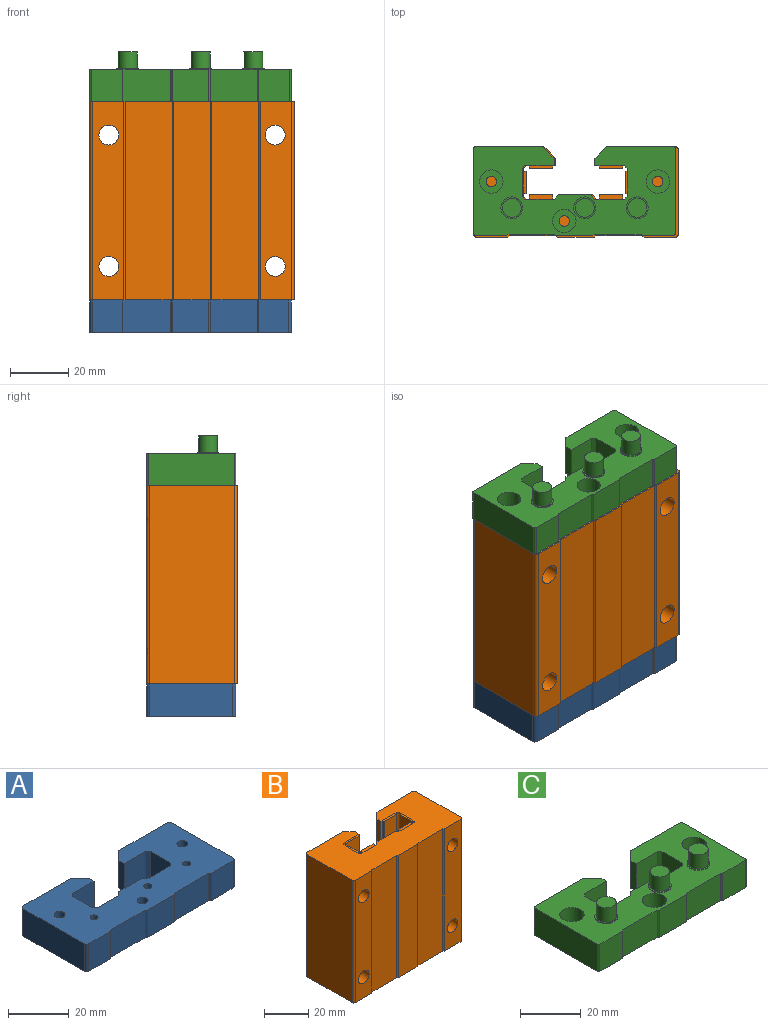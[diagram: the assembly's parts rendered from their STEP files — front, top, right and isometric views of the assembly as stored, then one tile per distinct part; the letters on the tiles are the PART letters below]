
ASSEMBLY  parts=3 mates=6
PART A: 51 faces, bbox 69x30.5x11 mm
  f0: cylinder r=1.8mm len=5mm, axis (0,0,1), area 56.5mm2, adj f49,f50
  f1: cylinder r=4mm len=8mm, axis (0,0,1), area 150.8mm2, adj f14,f50
  f2: cylinder r=1.8mm len=5mm, axis (0,0,1), area 56.5mm2, adj f13,f49
  f3: cylinder r=1.8mm len=5mm, axis (0,0,1), area 56.5mm2, adj f12,f49
  f4: cylinder r=1.3mm len=10mm, axis (0,0,1), area 81.7mm2, adj f7,f49
  f5: cylinder r=1.3mm len=10mm, axis (0,0,1), area 81.7mm2, adj f8,f49
  f6: cylinder r=1.3mm len=10mm, axis (0,0,1), area 81.7mm2, adj f9,f49
  f7: cone r=0.94mm half-angle=30deg, axis (0,0,-1), area 11.5mm2, adj f4,f14
  f8: cone r=0.94mm half-angle=30deg, axis (0,0,-1), area 11.5mm2, adj f5,f14
  f9: cone r=0.94mm half-angle=30deg, axis (0,0,-1), area 11.5mm2, adj f6,f14
  f10: cylinder r=4mm len=8mm, axis (0,0,1), area 150.8mm2, adj f13,f14
  f11: cylinder r=4mm len=8mm, axis (0,0,1), area 150.8mm2, adj f12,f14
  f12: plane 8x8mm, normal (0,0,-1), area 40.1mm2, adj f3,f11
  f13: plane 8x8mm, normal (0,0,-1), area 40.1mm2, adj f2,f10
  f14: plane 69x30.5mm, normal (0,0,-1), area 1402.9mm2, adj f1,f7,f8,f9,f10,f11,f15,f16
  f15: plane 11x2.5mm, normal (1,0,0), area 27.5mm2, adj f14,f16,f48,f49
  f16: plane 11x10mm, normal (0,-1,0), area 110mm2, adj f14,f15,f17,f49
  f17: plane 11x1mm, normal (0.71,-0.71,0), area 15.6mm2, adj f14,f16,f18,f49
  f18: plane 11x9.5mm, normal (1,0,0), area 104.5mm2, adj f14,f17,f19,f49
  f19: plane 11x1mm, normal (0.71,0.71,0), area 15.6mm2, adj f14,f18,f20,f49
  f20: plane 11x10mm, normal (0,1,0), area 110mm2, adj f14,f19,f21,f49
  f21: plane 11x1.5mm, normal (-0.71,0.71,0), area 23.3mm2, adj f14,f20,f22,f49
  f22: plane 11x11mm, normal (0,1,0), area 121mm2, adj f14,f21,f23,f49
  f23: plane 11x1.5mm, normal (0.71,0.71,0), area 23.3mm2, adj f14,f22,f24,f49
  f24: plane 11x10mm, normal (0,1,0), area 110mm2, adj f14,f23,f25,f49
  f25: plane 11x1mm, normal (-0.71,0.71,0), area 15.6mm2, adj f14,f24,f26,f49
  f26: plane 11x9.5mm, normal (-1,0,0), area 104.5mm2, adj f14,f25,f27,f49
  f27: plane 11x1mm, normal (-0.71,-0.71,0), area 15.6mm2, adj f14,f26,f28,f49
  f28: plane 11x10mm, normal (0,-1,0), area 110mm2, adj f14,f27,f29,f49
  f29: plane 11x2.5mm, normal (-1,0,0), area 27.5mm2, adj f14,f28,f30,f49
  f30: plane 11x4mm, normal (-0.71,0.71,0), area 62.2mm2, adj f14,f29,f31,f49
  f31: plane 22.5x11mm, normal (0,1,0), area 247.5mm2, adj f14,f30,f32,f49
  f32: cylinder r=1mm len=11mm, axis (0,0,1), area 17.3mm2, adj f14,f31,f33,f49
  f33: plane 28.5x11mm, normal (1,0,0), area 313.5mm2, adj f14,f32,f34,f49
  f34: cylinder r=1mm len=11mm, axis (0,0,1), area 17.3mm2, adj f14,f33,f35,f49
  f35: plane 11x10.2mm, normal (0,-1,0), area 112.2mm2, adj f14,f34,f36,f49
  f36: plane 11x0.5mm, normal (-0.71,-0.71,0), area 7.8mm2, adj f14,f35,f37,f49
  f37: plane 16x11mm, normal (0,-1,0), area 176mm2, adj f14,f36,f38,f49
  f38: plane 11x0.5mm, normal (0.71,-0.71,0), area 7.8mm2, adj f14,f37,f39,f49
  f39: plane 12.6x11mm, normal (0,-1,0), area 138.6mm2, adj f14,f38,f40,f49
  f40: plane 11x0.5mm, normal (-0.71,-0.71,0), area 7.8mm2, adj f14,f39,f41,f49
  f41: plane 16x11mm, normal (0,-1,0), area 176mm2, adj f14,f40,f42,f49
  f42: plane 11x0.5mm, normal (0.71,-0.71,0), area 7.8mm2, adj f14,f41,f43,f49
  f43: plane 11x10.2mm, normal (0,-1,0), area 112.2mm2, adj f14,f42,f44,f49
  f44: cylinder r=1mm len=11mm, axis (0,0,1), area 17.3mm2, adj f14,f43,f45,f49
  f45: plane 28.5x11mm, normal (-1,0,0), area 313.5mm2, adj f14,f44,f46,f49
  f46: cylinder r=1mm len=11mm, axis (0,0,1), area 17.3mm2, adj f14,f45,f47,f49
  f47: plane 22.5x11mm, normal (0,1,0), area 247.5mm2, adj f14,f46,f48,f49
  f48: plane 11x4mm, normal (0.71,0.71,0), area 62.2mm2, adj f14,f15,f47,f49
  f49: plane 69x30.5mm, normal (0,0,1), area 1540.4mm2, adj f0,f2,f3,f4,f5,f6,f15,f16
  f50: plane 8x8mm, normal (0,0,-1), area 40.1mm2, adj f0,f1
PART B: 78 faces, bbox 70x31x68 mm
  f0: cylinder r=6mm len=12mm, axis (0,-1,0), area 233.4mm2, adj f16,f40,f73
  f1: cylinder r=6mm len=12mm, axis (0,-1,0), area 233.4mm2, adj f15,f40,f73
  f2: cylinder r=6mm len=12mm, axis (0,-1,0), area 233.4mm2, adj f9,f54,f55
  f3: cylinder r=6mm len=12mm, axis (0,-1,0), area 233.4mm2, adj f8,f54,f55
  f4: cylinder r=3.4mm len=24.8mm, axis (0,-1,0), area 529.8mm2, adj f9,f51
  f5: cylinder r=3.4mm len=24.8mm, axis (0,-1,0), area 529.8mm2, adj f8,f51
  f6: cylinder r=3.4mm len=24.8mm, axis (0,-1,0), area 529.8mm2, adj f16,f43
  f7: cylinder r=3.4mm len=24.8mm, axis (0,-1,0), area 529.8mm2, adj f15,f43
  f8: plane 12x12mm, normal (0,1,0), area 76.8mm2, adj f3,f5
  f9: plane 12x12mm, normal (0,1,0), area 76.8mm2, adj f2,f4
  f10: plane 68x8mm, normal (0,-1,0), area 544mm2, adj f17,f18,f19,f20
  f11: plane 68x7.5mm, normal (1,0,0), area 510mm2, adj f21,f22,f23,f24
  f12: plane 68x8mm, normal (0,1,0), area 544mm2, adj f25,f26,f27,f28
  f13: plane 68x8mm, normal (0,1,0), area 544mm2, adj f29,f30,f31,f32
  f14: plane 68x8mm, normal (0,-1,0), area 544mm2, adj f33,f34,f35,f36
  f15: plane 12x12mm, normal (0,1,0), area 76.8mm2, adj f1,f7
  f16: plane 12x12mm, normal (0,1,0), area 76.8mm2, adj f0,f6
  f17: plane 8x1mm, normal (0,0,1), area 8mm2, adj f10,f19,f20,f77
  f18: plane 8x1mm, normal (0,0,-1), area 8mm2, adj f10,f19,f20,f58
  f19: plane 68x1mm, normal (1,0,0), area 68mm2, adj f10,f17,f18,f58
  f20: plane 68x1mm, normal (-1,0,0), area 68mm2, adj f10,f17,f18,f58
  f21: plane 7.5x1mm, normal (0,0,1), area 7.5mm2, adj f11,f23,f24,f77
  f22: plane 7.5x1mm, normal (0,0,-1), area 7.5mm2, adj f11,f23,f24,f60
  f23: plane 68x1mm, normal (0,1,0), area 68mm2, adj f11,f21,f22,f60
  f24: plane 68x1mm, normal (0,-1,0), area 68mm2, adj f11,f21,f22,f60
  f25: plane 8x1.5mm, normal (0,0,1), area 12mm2, adj f12,f27,f28,f77
  f26: plane 8x1.5mm, normal (0,0,-1), area 12mm2, adj f12,f27,f28,f62
  f27: plane 68x1.5mm, normal (-1,0,0), area 102mm2, adj f12,f25,f26,f62
  f28: plane 68x1.5mm, normal (1,0,0), area 102mm2, adj f12,f25,f26,f62
  f29: plane 8x1.5mm, normal (0,0,1), area 12mm2, adj f13,f31,f32,f77
  f30: plane 8x1.5mm, normal (0,0,-1), area 12mm2, adj f13,f31,f32,f66
  f31: plane 68x1.5mm, normal (-1,0,0), area 102mm2, adj f13,f29,f30,f66
  f32: plane 68x1.5mm, normal (1,0,0), area 102mm2, adj f13,f29,f30,f66
  f33: plane 8x1mm, normal (0,0,1), area 8mm2, adj f14,f35,f36,f77
  f34: plane 8x1mm, normal (0,0,-1), area 8mm2, adj f14,f35,f36,f70
  f35: plane 68x1mm, normal (1,0,0), area 68mm2, adj f14,f33,f34,f70
  f36: plane 68x1mm, normal (-1,0,0), area 68mm2, adj f14,f33,f34,f70
  f37: plane 70x31mm, normal (0,0,-1), area 1652.4mm2, adj f40,f41,f42,f43,f44,f45,f46,f47
  f38: plane 68x7.5mm, normal (-1,0,0), area 510mm2, adj f39,f74,f75,f76
  f39: plane 7.5x1mm, normal (0,0,-1), area 7.5mm2, adj f38,f68,f74,f76
  f40: cylinder r=1mm len=68mm, axis (0,0,-1), area 104.3mm2, adj f0,f1,f37,f41,f73,f77
  f41: plane 68x29mm, normal (1,0,0), area 1972mm2, adj f37,f40,f42,f77
  f42: cylinder r=1mm len=68mm, axis (0,0,-1), area 106.8mm2, adj f37,f41,f43,f77
  f43: plane 68x10.7mm, normal (0,-1,0), area 655mm2, adj f6,f7,f37,f42,f44,f77
  f44: plane 68x0.5mm, normal (-0.71,-0.71,0), area 48.1mm2, adj f37,f43,f45,f77
  f45: plane 68x16mm, normal (0,-1,0), area 1088mm2, adj f37,f44,f46,f77
  f46: plane 68x0.5mm, normal (0.71,-0.71,0), area 48.1mm2, adj f37,f45,f47,f77
  f47: plane 68x12.6mm, normal (0,-1,0), area 856.8mm2, adj f37,f46,f48,f77
  f48: plane 68x0.5mm, normal (-0.71,-0.71,0), area 48.1mm2, adj f37,f47,f49,f77
  f49: plane 68x16mm, normal (0,-1,0), area 1088mm2, adj f37,f48,f50,f77
  f50: plane 68x0.5mm, normal (0.71,-0.71,0), area 48.1mm2, adj f37,f49,f51,f77
  f51: plane 68x10.7mm, normal (0,-1,0), area 655mm2, adj f4,f5,f37,f50,f52,f77
  f52: cylinder r=1mm len=68mm, axis (0,0,-1), area 106.8mm2, adj f37,f51,f53,f77
  f53: plane 68x29mm, normal (-1,0,0), area 1972mm2, adj f37,f52,f54,f77
  f54: cylinder r=1mm len=68mm, axis (0,0,-1), area 104.3mm2, adj f2,f3,f37,f53,f55,f77
  f55: plane 68x23mm, normal (0,1,0), area 1341mm2, adj f2,f3,f37,f54,f56,f77
  f56: plane 68x4mm, normal (0.71,0.71,0), area 384.7mm2, adj f37,f55,f57,f77
  f57: plane 68x2.5mm, normal (1,0,0), area 170mm2, adj f37,f56,f58,f77
  f58: plane 68x10mm, normal (0,-1,0), area 136mm2, adj f18,f19,f20,f37,f57,f59,f77
  f59: plane 68x1mm, normal (0.71,-0.71,0), area 96.2mm2, adj f37,f58,f60,f77
  f60: plane 68x9.5mm, normal (1,0,0), area 136mm2, adj f22,f23,f24,f37,f59,f61,f77
  f61: plane 68x1mm, normal (0.71,0.71,0), area 96.2mm2, adj f37,f60,f62,f77
  f62: plane 68x10mm, normal (0,1,0), area 136mm2, adj f26,f27,f28,f37,f61,f63,f77
  f63: plane 68x1.5mm, normal (-0.71,0.71,0), area 144.2mm2, adj f37,f62,f64,f77
  f64: plane 68x11mm, normal (0,1,0), area 748mm2, adj f37,f63,f65,f77
  f65: plane 68x1.5mm, normal (0.71,0.71,0), area 144.2mm2, adj f37,f64,f66,f77
  f66: plane 68x10mm, normal (0,1,0), area 136mm2, adj f30,f31,f32,f37,f65,f67,f77
  f67: plane 68x1mm, normal (-0.71,0.71,0), area 96.2mm2, adj f37,f66,f68,f77
  f68: plane 68x9.5mm, normal (-1,0,0), area 136mm2, adj f37,f39,f67,f69,f74,f76,f77
  f69: plane 68x1mm, normal (-0.71,-0.71,0), area 96.2mm2, adj f37,f68,f70,f77
  f70: plane 68x10mm, normal (0,-1,0), area 136mm2, adj f34,f35,f36,f37,f69,f71,f77
  f71: plane 68x2.5mm, normal (-1,0,0), area 170mm2, adj f37,f70,f72,f77
  f72: plane 68x4mm, normal (-0.71,0.71,0), area 384.7mm2, adj f37,f71,f73,f77
  f73: plane 68x23mm, normal (0,1,0), area 1341mm2, adj f0,f1,f37,f40,f72,f77
  f74: plane 68x1mm, normal (0,-1,0), area 68mm2, adj f38,f39,f68,f75
  f75: plane 7.5x1mm, normal (0,0,1), area 7.5mm2, adj f38,f74,f76,f77
  f76: plane 68x1mm, normal (0,1,0), area 68mm2, adj f38,f39,f68,f75
  f77: plane 70x31mm, normal (0,0,1), area 1652.4mm2, adj f17,f21,f25,f29,f33,f40,f41,f42
PART C: 69 faces, bbox 69x30.5x17 mm
  f0: cylinder r=3.25mm len=6.5mm, axis (0,0,1), area 118.4mm2, adj f67,f68
  f1: cylinder r=3.75mm len=7.5mm, axis (0,0,1), area 4.7mm2, adj f66,f67
  f2: cylinder r=4mm len=8mm, axis (0,0,-1), area 150.8mm2, adj f31,f66
  f3: cylinder r=4mm len=8mm, axis (0,0,-1), area 150.8mm2, adj f30,f66
  f4: cylinder r=4mm len=8mm, axis (0,0,-1), area 150.8mm2, adj f29,f66
  f5: cylinder r=3.75mm len=7.5mm, axis (0,0,1), area 4.7mm2, adj f28,f66
  f6: cylinder r=3.75mm len=7.5mm, axis (0,0,1), area 4.7mm2, adj f27,f66
  f7: cylinder r=1.8mm len=5mm, axis (0,0,-1), area 56.5mm2, adj f26,f31
  f8: cylinder r=1.8mm len=5mm, axis (0,0,-1), area 56.5mm2, adj f26,f30
  f9: cylinder r=1.8mm len=5mm, axis (0,0,-1), area 56.5mm2, adj f26,f29
  f10: cylinder r=3.25mm len=6.5mm, axis (0,0,1), area 118.4mm2, adj f25,f28
  f11: cylinder r=3.25mm len=6.5mm, axis (0,0,1), area 118.4mm2, adj f24,f27
  f12: cylinder r=2.25mm len=5.2mm, axis (0,0,-1), area 73.5mm2, adj f23,f26
  f13: cylinder r=2.25mm len=5.2mm, axis (0,0,-1), area 73.5mm2, adj f22,f26
  f14: cylinder r=2.25mm len=5.2mm, axis (0,0,-1), area 73.5mm2, adj f21,f26
  f15: cylinder r=3.25mm len=6.5mm, axis (0,0,-1), area 118.4mm2, adj f20,f23
  f16: cylinder r=3.25mm len=6.5mm, axis (0,0,-1), area 118.4mm2, adj f19,f22
  f17: cylinder r=3.25mm len=6.5mm, axis (0,0,-1), area 118.4mm2, adj f18,f21
  f18: plane 6.5x6.5mm, normal (0,0,-1), area 33.2mm2, adj f17
  f19: plane 6.5x6.5mm, normal (0,0,-1), area 33.2mm2, adj f16
  f20: plane 6.5x6.5mm, normal (0,0,-1), area 33.2mm2, adj f15
  f21: plane 6.5x6.5mm, normal (0,0,1), area 17.3mm2, adj f14,f17
  f22: plane 6.5x6.5mm, normal (0,0,1), area 17.3mm2, adj f13,f16
  f23: plane 6.5x6.5mm, normal (0,0,1), area 17.3mm2, adj f12,f15
  f24: plane 6.5x6.5mm, normal (0,0,1), area 33.2mm2, adj f11
  f25: plane 6.5x6.5mm, normal (0,0,1), area 33.2mm2, adj f10
  f26: plane 69x30.5mm, normal (0,0,-1), area 1509.3mm2, adj f7,f8,f9,f12,f13,f14,f32,f33
  f27: plane 7.5x7.5mm, normal (0,0,1), area 11mm2, adj f6,f11
  f28: plane 7.5x7.5mm, normal (0,0,1), area 11mm2, adj f5,f10
  f29: plane 8x8mm, normal (0,0,1), area 40.1mm2, adj f4,f9
  f30: plane 8x8mm, normal (0,0,1), area 40.1mm2, adj f3,f8
  f31: plane 8x8mm, normal (0,0,1), area 40.1mm2, adj f2,f7
  f32: cylinder r=0.5mm len=11mm, axis (0,0,-1), area 8.6mm2, adj f26,f33,f65,f66
  f33: plane 29.5x11mm, normal (1,0,0), area 324.5mm2, adj f26,f32,f34,f66
  f34: cylinder r=0.5mm len=11mm, axis (0,0,-1), area 8.6mm2, adj f26,f33,f35,f66
  f35: plane 11x10.7mm, normal (0,-1,0), area 117.7mm2, adj f26,f34,f36,f66
  f36: plane 11x0.5mm, normal (-0.71,-0.71,0), area 7.8mm2, adj f26,f35,f37,f66
  f37: plane 16x11mm, normal (0,-1,0), area 176mm2, adj f26,f36,f38,f66
  f38: plane 11x0.5mm, normal (0.71,-0.71,0), area 7.8mm2, adj f26,f37,f39,f66
  f39: plane 12.6x11mm, normal (0,-1,0), area 138.6mm2, adj f26,f38,f40,f66
  f40: plane 11x0.5mm, normal (-0.71,-0.71,0), area 7.8mm2, adj f26,f39,f41,f66
  f41: plane 16x11mm, normal (0,-1,0), area 176mm2, adj f26,f40,f42,f66
  f42: plane 11x0.5mm, normal (0.71,-0.71,0), area 7.8mm2, adj f26,f41,f43,f66
  f43: plane 11x10.7mm, normal (0,-1,0), area 117.7mm2, adj f26,f42,f44,f66
  f44: cylinder r=0.5mm len=11mm, axis (0,0,-1), area 8.6mm2, adj f26,f43,f45,f66
  f45: plane 29.5x11mm, normal (-1,0,0), area 324.5mm2, adj f26,f44,f46,f66
  f46: cylinder r=0.5mm len=11mm, axis (0,0,-1), area 8.6mm2, adj f26,f45,f47,f66
  f47: plane 23x11mm, normal (0,1,0), area 253mm2, adj f26,f46,f48,f66
  f48: plane 11x4mm, normal (0.71,0.71,0), area 62.2mm2, adj f26,f47,f49,f66
  f49: plane 11x2.5mm, normal (1,0,0), area 27.5mm2, adj f26,f48,f50,f66
  f50: plane 11x10mm, normal (0,-1,0), area 110mm2, adj f26,f49,f51,f66
  f51: plane 11x1mm, normal (0.71,-0.71,0), area 15.6mm2, adj f26,f50,f52,f66
  f52: plane 11x9.5mm, normal (1,0,0), area 104.5mm2, adj f26,f51,f53,f66
  f53: plane 11x1mm, normal (0.71,0.71,0), area 15.6mm2, adj f26,f52,f54,f66
  f54: plane 11x10mm, normal (0,1,0), area 110mm2, adj f26,f53,f55,f66
  f55: plane 11x1.5mm, normal (-0.71,0.71,0), area 23.3mm2, adj f26,f54,f56,f66
  f56: plane 11x11mm, normal (0,1,0), area 121mm2, adj f26,f55,f57,f66
  f57: plane 11x1.5mm, normal (0.71,0.71,0), area 23.3mm2, adj f26,f56,f58,f66
  f58: plane 11x10mm, normal (0,1,0), area 110mm2, adj f26,f57,f59,f66
  f59: plane 11x1mm, normal (-0.71,0.71,0), area 15.6mm2, adj f26,f58,f60,f66
  f60: plane 11x9.5mm, normal (-1,0,0), area 104.5mm2, adj f26,f59,f61,f66
  f61: plane 11x1mm, normal (-0.71,-0.71,0), area 15.6mm2, adj f26,f60,f62,f66
  f62: plane 11x10mm, normal (0,-1,0), area 110mm2, adj f26,f61,f63,f66
  f63: plane 11x2.5mm, normal (-1,0,0), area 27.5mm2, adj f26,f62,f64,f66
  f64: plane 11x4mm, normal (-0.71,0.71,0), area 62.2mm2, adj f26,f63,f65,f66
  f65: plane 23x11mm, normal (0,1,0), area 253mm2, adj f26,f32,f64,f66
  f66: plane 69x30.5mm, normal (0,0,1), area 1304.2mm2, adj f1,f2,f3,f4,f5,f6,f32,f33
  f67: plane 7.5x7.5mm, normal (0,0,1), area 11mm2, adj f0,f1
  f68: plane 6.5x6.5mm, normal (0,0,1), area 33.2mm2, adj f0
PLACE A t=(13.76,-22.4,-108.01)mm
PLACE B t=(14.26,-22.4,-108.01)mm
PLACE C t=(13.76,-22.4,-108.01)mm
MATE planar C.f47 <-> B.f55  axis (0,1,0) through (-8.74,-22.9,-102.51)mm
MATE planar B.f37 <-> A.f49  axis (0,0,-1) through (14.26,-39.89,-176.01)mm
MATE planar B.f55 <-> A.f47  axis (0,1,0) through (-7.26,-22.9,-142.01)mm
MATE planar C.f45 <-> B.f53  axis (-1,0,0) through (-20.74,-38.15,-102.51)mm
MATE planar C.f45 <-> A.f45  axis (-1,0,0) through (-20.74,-38.15,-102.51)mm
MATE planar B.f77 <-> C.f26  axis (0,0,1) through (-20.74,-38.4,-108.01)mm
